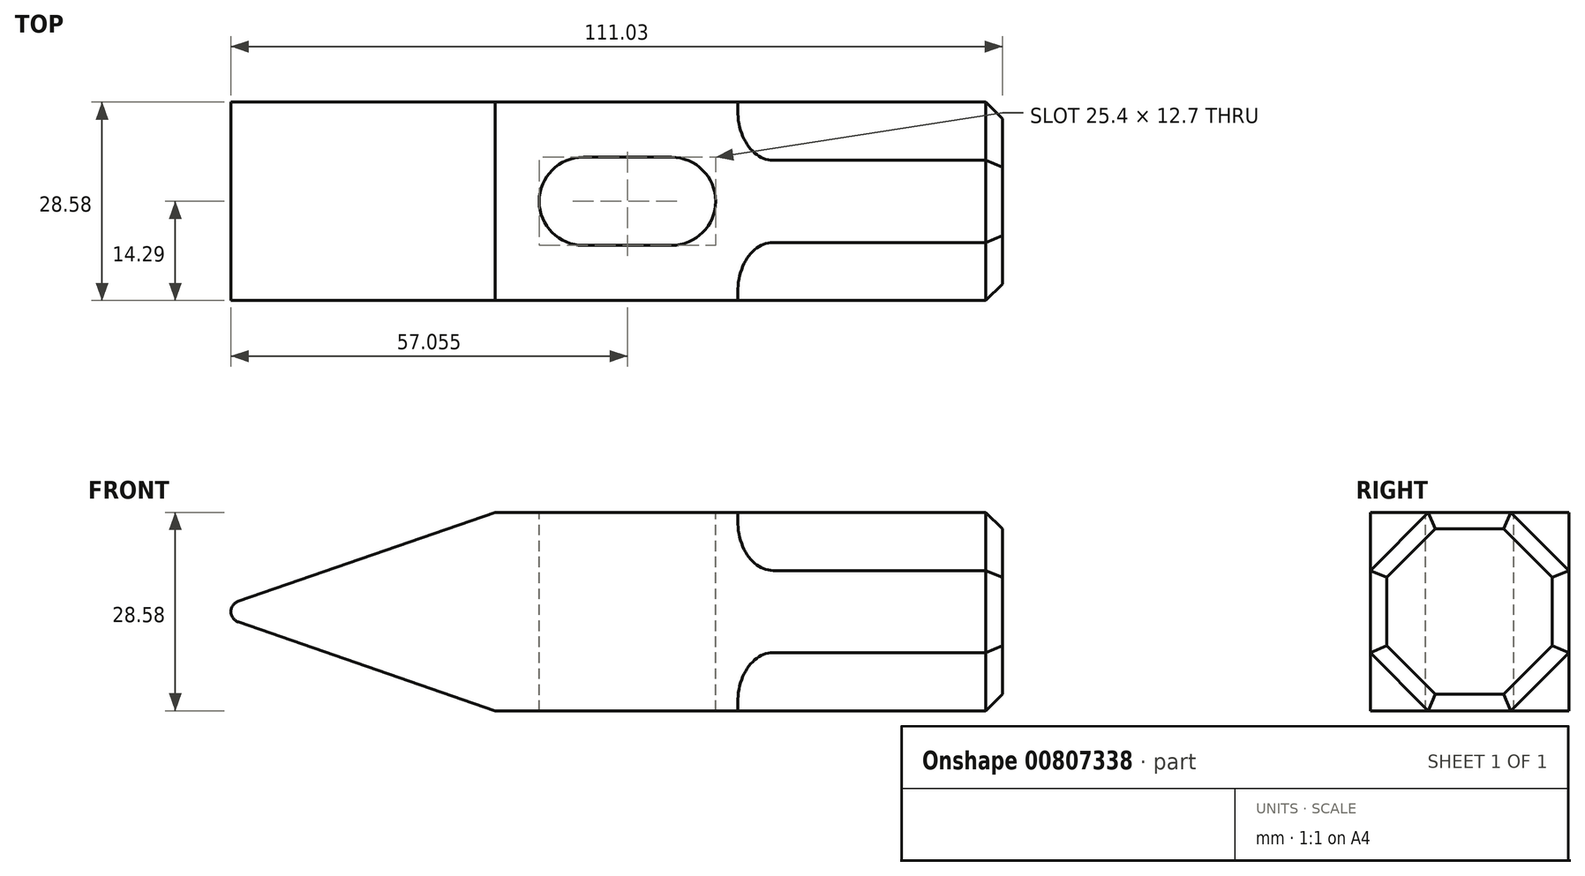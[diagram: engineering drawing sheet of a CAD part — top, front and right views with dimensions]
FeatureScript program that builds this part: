
annotation { "Feature Type Name" : "Feature", "Feature Type Description" : "" }
export const myFeature = defineFeature(function(context is Context, id is Id, definition is map)
    precondition{}
    {
        {
            var Q0;
            Q0=qCreatedBy(makeId("Front.planeOp"),FACE);
            var sketch = newSketch(context, id + "F0", { "sketchPlane" : qUnion([Q0])});
            skLineSegment(sketch, "E0", {"start": v(0, 0) * mm, "end": v(114.3, 0) * mm, "construction": true});
            skLineSegment(sketch, "E1", {"start": v(41.28, 14.29) * mm, "end": v(41.28, -14.29) * mm, "construction": true});
            skPoint(sketch, "E2", {"position": v(41.28, 0) * mm});
            skLineSegment(sketch, "E3", {"start": v(41.28, 14.29) * mm, "end": v(4.33, 1.5) * mm});
            skLineSegment(sketch, "E4", {"start": v(4.33, -1.5) * mm, "end": v(41.28, -14.29) * mm});
            skLineSegment(sketch, "E5", {"start": v(76.2, 14.29) * mm, "end": v(76.2, -14.29) * mm, "construction": true});
            skPoint(sketch, "E6", {"position": v(76.2, 0) * mm});
            skLineSegment(sketch, "E7", {"start": v(41.28, 14.29) * mm, "end": v(76.2, 14.29) * mm});
            skLineSegment(sketch, "E8", {"start": v(41.28, -14.29) * mm, "end": v(76.2, -14.29) * mm});
            skLineSegment(sketch, "E9", {"start": v(76.2, 14.29) * mm, "end": v(114.3, 14.29) * mm});
            skLineSegment(sketch, "E10", {"start": v(114.3, 14.29) * mm, "end": v(114.3, -14.29) * mm});
            skLineSegment(sketch, "E11", {"start": v(114.3, -14.29) * mm, "end": v(76.2, -14.29) * mm});
            skPoint(sketch, "E12.visualSharp", {"position": v(0, 0) * mm});
            skArc(sketch, "E12.filletArc", {"start": v(4.33, 1.5) * mm, "mid": v(3.27, 0) * mm, "end": v(4.33, -1.5) * mm});
            skSolve(sketch);
        }
        {
            var Q0;
            Q0=makeQuery(id+"F0.imprint","IMPRINT",FACE,{"disambiguationData":[TD([[makeQuery(id+"F0.imprint","IMPRINT",EDGE,{"derivedFrom":sQuery(id+"F0.wireOp",EDGE,"E3")}),1.0]])]});
            extrude(context, id + "F1", {"entities" : qUnion([Q0]), "endBound" : BoundingType.SYMMETRIC, "depth" : 28.57 * mm, "offsetDistance" : 25.4 * mm});
        }
        {
            var Q0;
            Q0=makeQuery(id+"F1.opExtrude","SWEPT_FACE",FACE,{"disambiguationData":[OSD([sQuery(id+"F0.wireOp",EDGE,"E7"),sQuery(id+"F0.wireOp",EDGE,"E9")])]});
            var sketch = newSketch(context, id + "F2", { "sketchPlane" : qUnion([Q0])});
            skPoint(sketch, "E13.0", {"position": v(114.3, 0) * mm});
            skPoint(sketch, "E14.0", {"position": v(77.79, 14.29) * mm});
            skPoint(sketch, "E15.0", {"position": v(77.79, -14.29) * mm});
            skPoint(sketch, "E16.0", {"position": v(41.28, 0) * mm});
            skLineSegment(sketch, "E17", {"start": v(53.98, 6.35) * mm, "end": v(66.68, 6.35) * mm});
            skLineSegment(sketch, "E18", {"start": v(66.68, -6.35) * mm, "end": v(53.98, -6.35) * mm});
            skArc(sketch, "E19", {"start": v(53.98, 6.35) * mm, "mid": v(47.63, 0) * mm, "end": v(53.98, -6.35) * mm});
            skArc(sketch, "E20", {"start": v(53.98, -6.35) * mm, "mid": v(60.33, 0) * mm, "end": v(53.98, 6.35) * mm, "construction": true});
            skArc(sketch, "E21", {"start": v(66.68, -6.35) * mm, "mid": v(73.03, 0) * mm, "end": v(66.68, 6.35) * mm});
            skArc(sketch, "E22", {"start": v(66.68, 6.35) * mm, "mid": v(60.33, 0) * mm, "end": v(66.68, -6.35) * mm, "construction": true});
            skSolve(sketch);
        }
        {
            var Q0;
            Q0=makeQuery(id+"F2.imprint","IMPRINT",FACE,{"disambiguationData":[TD([[makeQuery(id+"F2.imprint","IMPRINT",EDGE,{"derivedFrom":sQuery(id+"F2.wireOp",EDGE,"E17")}),-1.0]])]});
            extrude(context, id + "F3", {"entities" : qUnion([Q0]), "operationType" : NewBodyOperationType.REMOVE, "endBound" : BoundingType.THROUGH_ALL, "oppositeDirection" : true, "depth" : 25.4 * mm, "offsetDistance" : 25.4 * mm});
        }
        {
            var Q0;
            Q0=makeQuery(id+"F1.opExtrude","SWEPT_FACE",FACE,{"disambiguationData":[OSD([sQuery(id+"F0.wireOp",EDGE,"E10")])]});
            var sketch = newSketch(context, id + "F4", { "sketchPlane" : qUnion([Q0])});
            skLineSegment(sketch, "E23.0.0", {"start": v(14.29, -14.29) * mm, "end": v(14.29, 14.29) * mm});
            skLineSegment(sketch, "E23.0.1", {"start": v(14.29, 14.29) * mm, "end": v(-14.29, 14.29) * mm});
            skLineSegment(sketch, "E23.0.2", {"start": v(-14.29, 14.29) * mm, "end": v(-14.29, -14.29) * mm});
            skLineSegment(sketch, "E23.0.3", {"start": v(-14.29, -14.29) * mm, "end": v(14.29, -14.29) * mm});
            skPoint(sketch, "E24.0", {"position": v(0, 0) * mm});
            skCircle(sketch, "E25.cCircle", {"center": v(0, 0) * mm, "radius": 15.46 * mm, "construction": true});
            skLineSegment(sketch, "E25.0", {"start": v(14.29, -5.92) * mm, "end": v(5.92, -14.29) * mm});
            skLineSegment(sketch, "E25.1", {"start": v(5.92, -14.29) * mm, "end": v(-5.92, -14.29) * mm});
            skLineSegment(sketch, "E25.2", {"start": v(-5.92, -14.29) * mm, "end": v(-14.29, -5.92) * mm});
            skLineSegment(sketch, "E25.3", {"start": v(-14.29, -5.92) * mm, "end": v(-14.29, 5.92) * mm});
            skLineSegment(sketch, "E25.4", {"start": v(-14.29, 5.92) * mm, "end": v(-5.92, 14.29) * mm});
            skLineSegment(sketch, "E25.5", {"start": v(-5.92, 14.29) * mm, "end": v(5.92, 14.29) * mm});
            skLineSegment(sketch, "E25.6", {"start": v(5.92, 14.29) * mm, "end": v(14.29, 5.92) * mm});
            skLineSegment(sketch, "E25.7", {"start": v(14.29, 5.92) * mm, "end": v(14.29, -5.92) * mm});
            skSolve(sketch);
        }
        {
            var Q0;
            {var subQ3=sQuery(id+"F4.wireOp",EDGE,"E25.6");Q0=makeQuery(id+"F4.imprint","IMPRINT",FACE,{"disambiguationData":[TD([[makeQuery(id+"F4.imprint","IMPRINT",EDGE,{"derivedFrom":subQ3}),1.0]])]});}
            var Q1;
            {var subQ3=sQuery(id+"F4.wireOp",EDGE,"E25.4");Q1=makeQuery(id+"F4.imprint","IMPRINT",FACE,{"disambiguationData":[TD([[makeQuery(id+"F4.imprint","IMPRINT",EDGE,{"derivedFrom":subQ3}),1.0]])]});}
            var Q2;
            {var subQ3=sQuery(id+"F4.wireOp",EDGE,"E25.2");Q2=makeQuery(id+"F4.imprint","IMPRINT",FACE,{"disambiguationData":[TD([[makeQuery(id+"F4.imprint","IMPRINT",EDGE,{"derivedFrom":subQ3}),1.0]])]});}
            var Q3;
            {var subQ3=sQuery(id+"F4.wireOp",EDGE,"E25.0");Q3=makeQuery(id+"F4.imprint","IMPRINT",FACE,{"disambiguationData":[TD([[makeQuery(id+"F4.imprint","IMPRINT",EDGE,{"derivedFrom":subQ3}),1.0]])]});}
            extrude(context, id + "F5", {"entities" : qUnion([Q0, Q1, Q2, Q3]), "operationType" : NewBodyOperationType.REMOVE, "oppositeDirection" : true, "depth" : 38.1 * mm, "offsetDistance" : 25.4 * mm});
        }
        {
            var Q0;
            Q0=makeQuery(id+"F5.boolean.opBoolean","COPY",EDGE,{"derivedFrom":makeQuery(id+"F5.opExtrude","CAP_EDGE",EDGE,{"disambiguationData":[OSD([sQuery(id+"F4.wireOp",EDGE,"E25.4")])],"isStart":false})});
            var Q1;
            Q1=makeQuery(id+"F5.boolean.opBoolean","COPY",EDGE,{"derivedFrom":makeQuery(id+"F5.opExtrude","CAP_EDGE",EDGE,{"disambiguationData":[OSD([sQuery(id+"F4.wireOp",EDGE,"E25.2")])],"isStart":false})});
            var Q2;
            Q2=makeQuery(id+"F5.boolean.opBoolean","COPY",EDGE,{"derivedFrom":makeQuery(id+"F5.opExtrude","CAP_EDGE",EDGE,{"disambiguationData":[OSD([sQuery(id+"F4.wireOp",EDGE,"E25.0")])],"isStart":false})});
            var Q3;
            Q3=makeQuery(id+"F5.boolean.opBoolean","COPY",EDGE,{"derivedFrom":makeQuery(id+"F5.opExtrude","CAP_EDGE",EDGE,{"disambiguationData":[OSD([sQuery(id+"F4.wireOp",EDGE,"E25.6")])],"isStart":false})});
            fillet(context, id + "F6", {"entities" : qUnion([Q0, Q1, Q2, Q3]), "radius" : 5.08 * mm, "tangentPropagation" : true, "allowEdgeOverflow" : false});
        }
        {
            var Q0;
            Q0=makeQuery(id+"F1.opExtrude","SWEPT_FACE",FACE,{"disambiguationData":[OSD([sQuery(id+"F0.wireOp",EDGE,"E10")])]});
            chamfer(context, id + "F7", {"entities" : qUnion([Q0]), "width" : 2.38 * mm, "tangentPropagation" : true});
        }
    });
